# Revit family: S-754
name_source: partatom
category: Aparatos sanitarios
revit_build: Autodesk Revit 2015 (Build: 20140606_1530(x64)
units: mm (PartAtom-declared; Revit-internal decimal feet)

## types (6) — shared parameters
B = 52 mm
Comentarios de tipo = COMPATIBLE CON CERCOS VISTOS Y OCULTOS
Descripción = REJILLA PARA CANALETA, SQUARE, PARA CANALETAS ANCHO 50
Fabricante = Jimten
Material = INOX AISI304
Modelo = S-754
Rejilla = INOX AISI304
URL = http://www.jimten.com
zero-valued in all types: Costo

## per-type parameters (varying)
| type | A | Medida | N_MatrizHuecos | Referencia |
| 50x350mm_SQUARE | 340 mm  [stored 1.11549 ft] | 350mm x 50mm | 4 | 13537 |
| 50x550mm_SQUARE | 540 mm | 550mm x 50mm | 6 | 13557 |
| 50x650mm_SQUARE | 640 mm  [stored 2.09974 ft] | 650mm x 50mm | 7 | 13567 |
| 50x750mm_SQUARE | 740 mm | 750mm x 50mm | 8 | 13577 |
| 50x850mm_SQUARE | 840 mm | 850mm x 50mm | 9 | 13587 |
| 50x950mm_SQUARE | 940 mm | 950mm x 50mm | 10 | 13597 |

note: [stored X ft] marks values corroborated as IEEE doubles in the binary element streams (Revit-internal decimal feet)

## geometry (parser evidence)
native form markers: Blend x6, Sweep x2
no freeform markers — native parametric forms only
